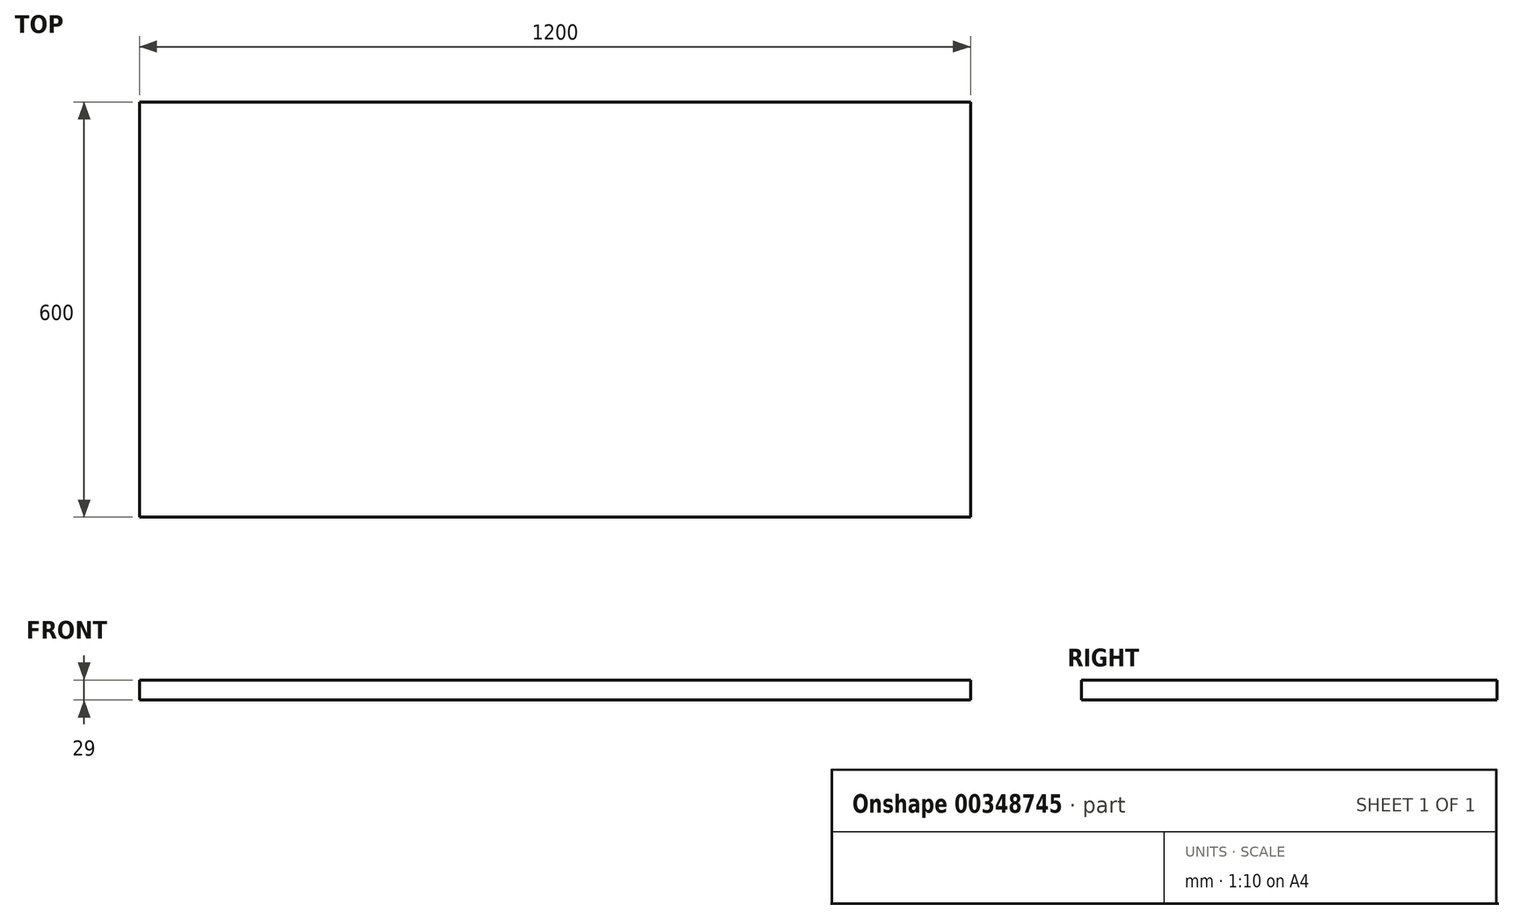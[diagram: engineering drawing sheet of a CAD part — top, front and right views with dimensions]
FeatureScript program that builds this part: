
annotation { "Feature Type Name" : "Feature", "Feature Type Description" : "" }
export const myFeature = defineFeature(function(context is Context, id is Id, definition is map)
    precondition{}
    {
        {
            var Q0;
            Q0=qCreatedBy(makeId("Top.planeOp"),FACE);
            var sketch = newSketch(context, id + "F0", { "sketchPlane" : qUnion([Q0])});
            skLineSegment(sketch, "E0.bottom", {"start": v(-600, 300) * mm, "end": v(600, 300) * mm});
            skLineSegment(sketch, "E0.top", {"start": v(-600, -300) * mm, "end": v(600, -300) * mm});
            skLineSegment(sketch, "E0.left", {"start": v(-600, 300) * mm, "end": v(-600, -300) * mm});
            skLineSegment(sketch, "E0.right", {"start": v(600, 300) * mm, "end": v(600, -300) * mm});
            skPoint(sketch, "E0.middle", {"position": v(0, 0) * mm});
            skSolve(sketch);
        }
        {
            var Q0;
            Q0=makeQuery(id+"F0.imprint","IMPRINT",FACE,{"disambiguationData":[TD([[makeQuery(id+"F0.imprint","IMPRINT",EDGE,{"derivedFrom":sQuery(id+"F0.wireOp",EDGE,"E0.bottom")}),-1.0]])]});
            extrude(context, id + "F1", {"entities" : qUnion([Q0]), "depth" : 29 * mm});
        }
    });
